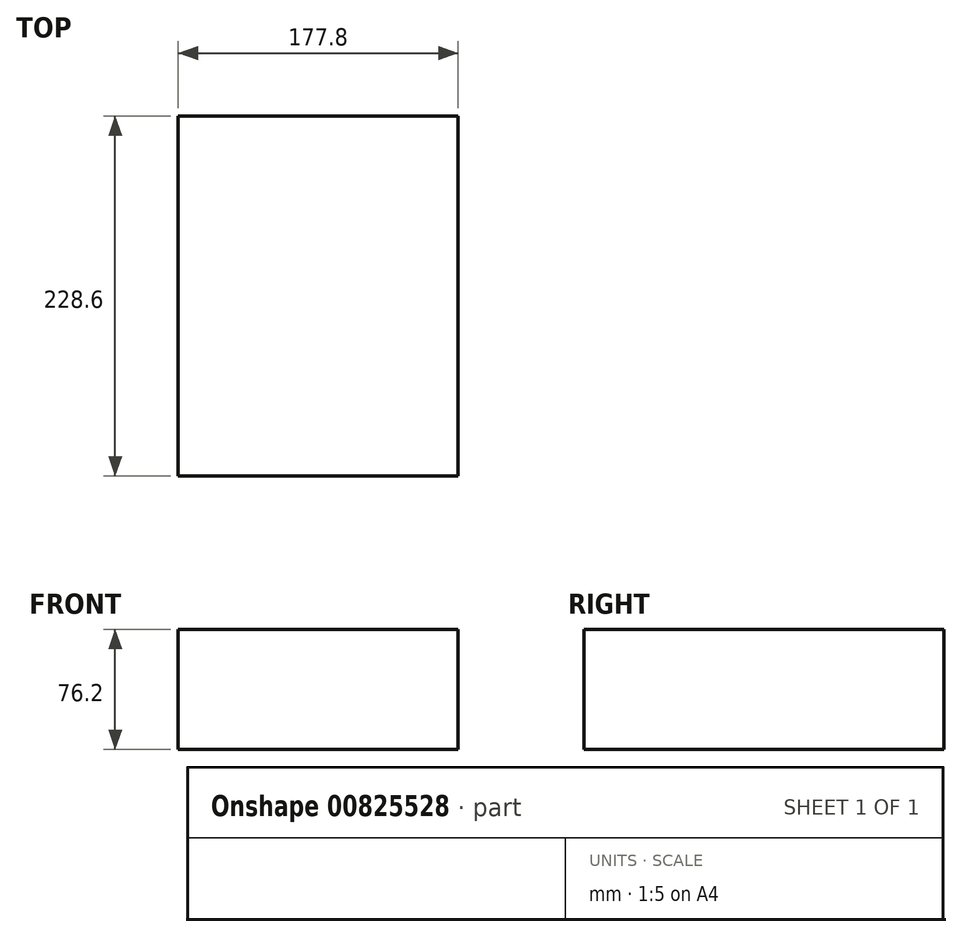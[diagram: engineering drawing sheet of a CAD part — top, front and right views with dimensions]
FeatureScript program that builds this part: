
annotation { "Feature Type Name" : "Feature", "Feature Type Description" : "" }
export const myFeature = defineFeature(function(context is Context, id is Id, definition is map)
    precondition{}
    {
        {
            var Q0;
            Q0=qCreatedBy(makeId("Top.planeOp"),FACE);
            var sketch = newSketch(context, id + "F0", { "sketchPlane" : qUnion([Q0])});
            skLineSegment(sketch, "E0.bottom", {"start": v(-87.74, 137.06) * mm, "end": v(90.06, 137.06) * mm});
            skLineSegment(sketch, "E0.top", {"start": v(-87.74, -91.54) * mm, "end": v(90.06, -91.54) * mm});
            skLineSegment(sketch, "E0.left", {"start": v(-87.74, 137.06) * mm, "end": v(-87.74, -91.54) * mm});
            skLineSegment(sketch, "E0.right", {"start": v(90.06, 137.06) * mm, "end": v(90.06, -91.54) * mm});
            skSolve(sketch);
        }
        {
            var Q0;
            Q0=makeQuery(id+"F0.imprint","IMPRINT",FACE,{"disambiguationData":[TD([[makeQuery(id+"F0.imprint","IMPRINT",EDGE,{"derivedFrom":sQuery(id+"F0.wireOp",EDGE,"E0.bottom")}),-1.0]])]});
            extrude(context, id + "F1", {"entities" : qUnion([Q0]), "depth" : 76.2 * mm, "offsetDistance" : 25.4 * mm});
        }
    });
